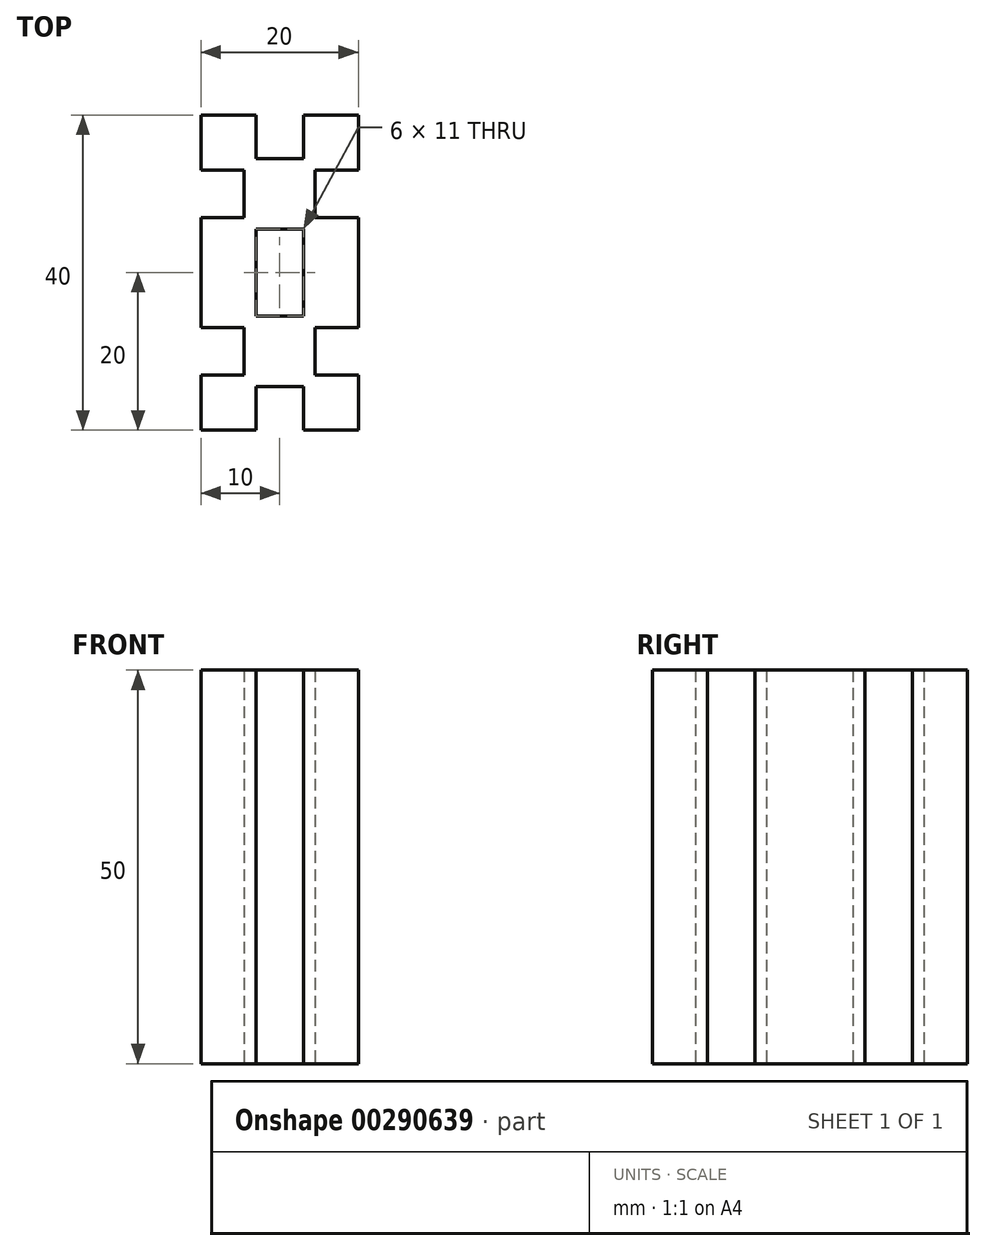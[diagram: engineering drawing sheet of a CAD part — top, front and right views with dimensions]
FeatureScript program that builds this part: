
annotation { "Feature Type Name" : "Feature", "Feature Type Description" : "" }
export const myFeature = defineFeature(function(context is Context, id is Id, definition is map)
    precondition{}
    {
        {
            var Q0;
            Q0=qCreatedBy(makeId("Top.planeOp"),FACE);
            var sketch = newSketch(context, id + "F0", { "sketchPlane" : qUnion([Q0])});
            skLineSegment(sketch, "E0.bottom", {"start": v(0, 0) * mm, "end": v(7, 0) * mm});
            skLineSegment(sketch, "E0.top", {"start": v(0, 20) * mm, "end": v(20, 20) * mm});
            skLineSegment(sketch, "E0.left", {"start": v(0, 0) * mm, "end": v(0, 20) * mm});
            skLineSegment(sketch, "E0.right", {"start": v(20, 0) * mm, "end": v(20, 20) * mm});
            skLineSegment(sketch, "E1.bottom", {"start": v(7, 20) * mm, "end": v(13, 20) * mm});
            skLineSegment(sketch, "E1.top", {"start": v(7, 14.5) * mm, "end": v(13, 14.5) * mm});
            skLineSegment(sketch, "E1.left", {"start": v(7, 20) * mm, "end": v(7, 14.5) * mm});
            skLineSegment(sketch, "E1.right", {"start": v(13, 20) * mm, "end": v(13, 14.5) * mm});
            skLineSegment(sketch, "E2.bottom", {"start": v(20, 13) * mm, "end": v(14.5, 13) * mm});
            skLineSegment(sketch, "E2.top", {"start": v(20, 7) * mm, "end": v(14.5, 7) * mm});
            skLineSegment(sketch, "E2.left", {"start": v(20, 13) * mm, "end": v(20, 7) * mm});
            skLineSegment(sketch, "E2.right", {"start": v(14.5, 13) * mm, "end": v(14.5, 7) * mm});
            skLineSegment(sketch, "E3.top", {"start": v(13, 5.5) * mm, "end": v(7, 5.5) * mm});
            skLineSegment(sketch, "E3.left", {"start": v(13, 0) * mm, "end": v(13, 5.5) * mm});
            skLineSegment(sketch, "E3.right", {"start": v(7, 0) * mm, "end": v(7, 5.5) * mm});
            skLineSegment(sketch, "E4.bottom", {"start": v(0, 7) * mm, "end": v(5.5, 7) * mm});
            skLineSegment(sketch, "E4.top", {"start": v(0, 13) * mm, "end": v(5.5, 13) * mm});
            skLineSegment(sketch, "E4.left", {"start": v(0, 7) * mm, "end": v(0, 13) * mm});
            skLineSegment(sketch, "E4.right", {"start": v(5.5, 7) * mm, "end": v(5.5, 13) * mm});
            skLineSegment(sketch, "E5.MirrorCS", {"start": v(5.5, -7) * mm, "end": v(5.5, -13) * mm});
            skLineSegment(sketch, "E6.MirrorCS", {"start": v(13, -5.5) * mm, "end": v(7, -5.5) * mm});
            skLineSegment(sketch, "E7.MirrorCS", {"start": v(0, -20) * mm, "end": v(20, -20) * mm});
            skLineSegment(sketch, "E8.MirrorCS", {"start": v(7, -20) * mm, "end": v(13, -20) * mm});
            skLineSegment(sketch, "E9.MirrorCS", {"start": v(7, -14.5) * mm, "end": v(13, -14.5) * mm});
            skLineSegment(sketch, "E10.MirrorCS", {"start": v(7, -20) * mm, "end": v(7, -14.5) * mm});
            skLineSegment(sketch, "E11.MirrorCS", {"start": v(13, -20) * mm, "end": v(13, -14.5) * mm});
            skLineSegment(sketch, "E12.MirrorCS", {"start": v(20, -13) * mm, "end": v(14.5, -13) * mm});
            skLineSegment(sketch, "E13.MirrorCS", {"start": v(20, -7) * mm, "end": v(14.5, -7) * mm});
            skLineSegment(sketch, "E14.MirrorCS", {"start": v(20, -13) * mm, "end": v(20, -7) * mm});
            skLineSegment(sketch, "E15.MirrorCS", {"start": v(14.5, -13) * mm, "end": v(14.5, -7) * mm});
            skLineSegment(sketch, "E16.MirrorCS", {"start": v(0, -7) * mm, "end": v(5.5, -7) * mm});
            skLineSegment(sketch, "E17.MirrorCS", {"start": v(0, -13) * mm, "end": v(5.5, -13) * mm});
            skLineSegment(sketch, "E18.MirrorCS", {"start": v(0, -7) * mm, "end": v(0, -13) * mm});
            skLineSegment(sketch, "E19.MirrorCS", {"start": v(7, 0) * mm, "end": v(7, -5.5) * mm});
            skLineSegment(sketch, "E20.MirrorCS", {"start": v(20, 0) * mm, "end": v(20, -20) * mm});
            skLineSegment(sketch, "E21.MirrorCS", {"start": v(0, 0) * mm, "end": v(0, -20) * mm});
            skLineSegment(sketch, "E22.MirrorCS", {"start": v(13, 0) * mm, "end": v(13, -5.5) * mm});
            skLineSegment(sketch, "E23.trimOffspring", {"start": v(13, 0) * mm, "end": v(20, 0) * mm});
            skSolve(sketch);
        }
        {
            var Q0;
            Q0=makeQuery(id+"F0.imprint","IMPRINT",FACE,{"disambiguationData":[TD([[makeQuery(id+"F0.imprint","IMPRINT",EDGE,{"derivedFrom":sQuery(id+"F0.wireOp",EDGE,"E1.top")}),-1.0]])]});
            var Q1;
            {var subQ8=sQuery(id+"F0.wireOp",EDGE,"E0.bottom");Q1=makeQuery(id+"F0.imprint","IMPRINT",FACE,{"disambiguationData":[TD([[makeQuery(id+"F0.imprint","IMPRINT",EDGE,{"derivedFrom":subQ8}),-1.0]])]});}
            extrude(context, id + "F1", {"entities" : qUnion([Q0, Q1]), "depth" : 50 * mm});
        }
    });
